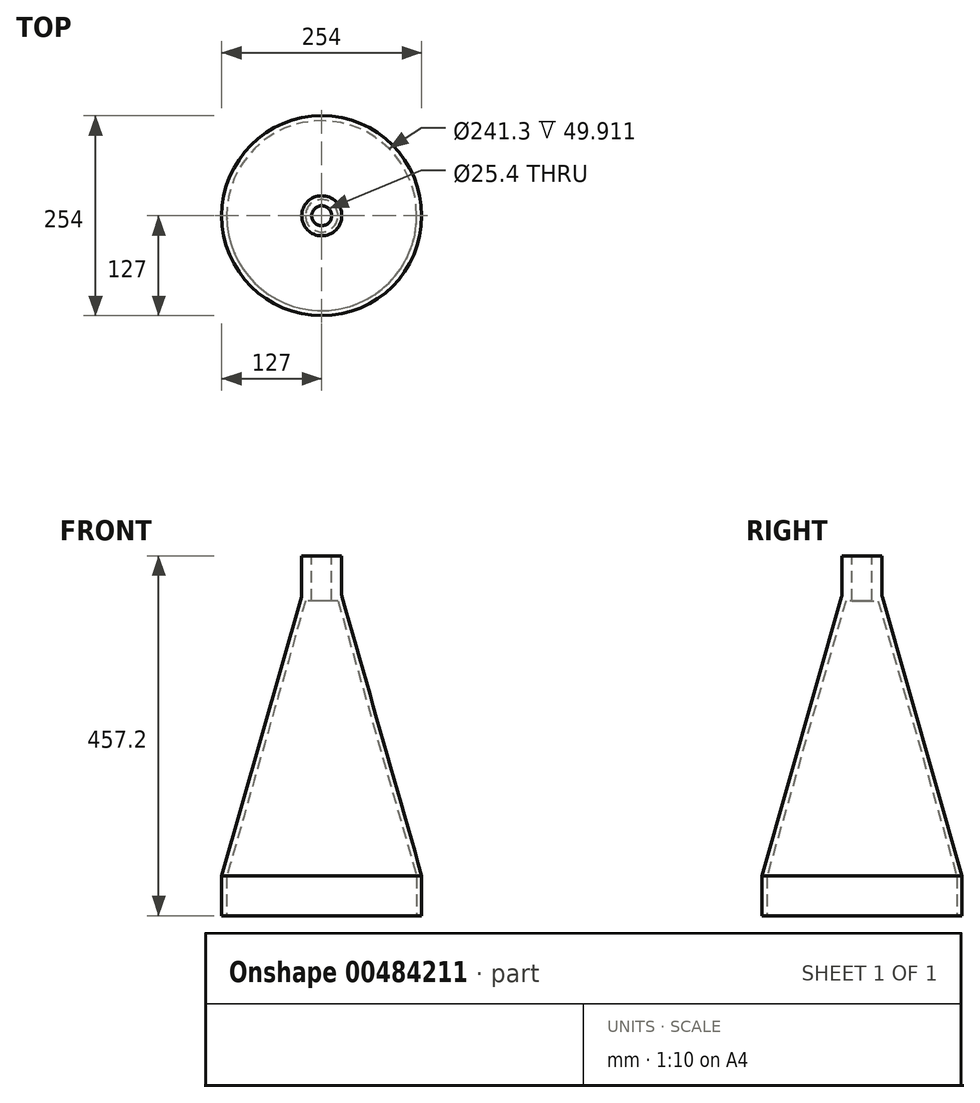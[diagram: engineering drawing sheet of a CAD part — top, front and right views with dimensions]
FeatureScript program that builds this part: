
annotation { "Feature Type Name" : "Feature", "Feature Type Description" : "" }
export const myFeature = defineFeature(function(context is Context, id is Id, definition is map)
    precondition{}
    {
        {
            var Q0;
            Q0=qCreatedBy(makeId("Top.planeOp"),FACE);
            var sketch = newSketch(context, id + "F0", { "sketchPlane" : qUnion([Q0])});
            skCircle(sketch, "E0", {"center": v(0, 0) * mm, "radius": 127 * mm});
            skSolve(sketch);
        }
        {
            var Q0;
            Q0 = qSketchRegion(id + "F0", true);
            extrude(context, id + "F1", {"entities" : qUnion([Q0]), "depth" : 406.4 * mm});
        }
        {
            var Q0;
            Q0=makeQuery(id+"F1.opExtrude","CAP_FACE",FACE,{"disambiguationData":[OSD([sQuery(id+"F0.wireOp",EDGE,"E0")])],"isStart":false});
            chamfer(context, id + "F2", {"entities" : qUnion([Q0]), "chamferType" : ChamferType.TWO_OFFSETS, "width1" : 101.6 * mm, "oppositeDirection" : false, "width2" : 355.6 * mm});
        }
        {
            var Q0;
            Q0=makeQuery(id+"F1.opExtrude","CAP_FACE",FACE,{"disambiguationData":[OSD([sQuery(id+"F0.wireOp",EDGE,"E0")])],"isStart":true});
            shell(context, id + "F3", {"entities" : qUnion([Q0]), "thickness" : 6.35 * mm});
        }
        {
            var Q0;
            Q0=makeQuery(id+"F1.opExtrude","CAP_FACE",FACE,{"disambiguationData":[OSD([sQuery(id+"F0.wireOp",EDGE,"E0")])],"isStart":false});
            var sketch = newSketch(context, id + "F4", { "sketchPlane" : qUnion([Q0])});
            skCircle(sketch, "E1", {"center": v(0, 0) * mm, "radius": 12.7 * mm});
            skSolve(sketch);
        }
        {
            var Q0;
            Q0 = qSketchRegion(id + "F4", true);
            extrude(context, id + "F5", {"entities" : qUnion([Q0]), "operationType" : NewBodyOperationType.REMOVE, "oppositeDirection" : true, "depth" : 25.4 * mm});
        }
        {
            var Q0;
            Q0=makeQuery(id+"F1.opExtrude","CAP_FACE",FACE,{"disambiguationData":[OSD([sQuery(id+"F0.wireOp",EDGE,"E0")])],"isStart":false});
            var sketch = newSketch(context, id + "F6", { "sketchPlane" : qUnion([Q0])});
            skCircle(sketch, "E2", {"center": v(0, 0) * mm, "radius": 25.4 * mm});
            skPoint(sketch, "E2.first.point", {"position": v(-11.01, 22.89) * mm});
            skPoint(sketch, "E2.second.point", {"position": v(25.25, -2.75) * mm});
            skPoint(sketch, "E2.third.point", {"position": v(-12.56, -22.08) * mm});
            skCircle(sketch, "E3", {"center": v(0, 0) * mm, "radius": 12.7 * mm});
            skPoint(sketch, "E3.first.point", {"position": v(-6.77, 10.74) * mm});
            skPoint(sketch, "E3.second.point", {"position": v(12.7, 0) * mm});
            skPoint(sketch, "E3.third.point", {"position": v(-9.08, -8.88) * mm});
            skSolve(sketch);
        }
        {
            var Q0;
            Q0 = qSketchRegion(id + "F6", true);
            extrude(context, id + "F7", {"entities" : qUnion([Q0]), "operationType" : NewBodyOperationType.ADD, "depth" : 50.8 * mm});
        }
        {
            var Q0;
            {var subQ0=sQuery(id+"F0.wireOp",EDGE,"E0");Q0=makeQuery(id+"F7.boolean.opBoolean","MERGE",EDGE,{"derivedFrom":[makeQuery(id+"F2.opChamfer","BLEND_EDGE",EDGE,{"blendedFrom":[makeQuery(id+"F1.opExtrude","CAP_EDGE",EDGE,{"disambiguationData":[OSD([subQ0])],"isStart":false}),makeQuery(id+"F1.opExtrude","CAP_FACE",FACE,{"disambiguationData":[OSD([subQ0])],"isStart":false})],"blendedInto":[makeQuery(id+"F1.opExtrude","CAP_FACE",FACE,{"disambiguationData":[OSD([subQ0])],"isStart":false})]}),makeQuery(id+"F7.opExtrude","CAP_EDGE",EDGE,{"disambiguationData":[OSD([sQuery(id+"F6.wireOp",EDGE,"E2")])],"isStart":true})]});}
            fillet(context, id + "F8", {"entities" : qUnion([Q0]), "radius" : 12.7 * mm, "tangentPropagation" : true, "allowEdgeOverflow" : false});
        }
    });
